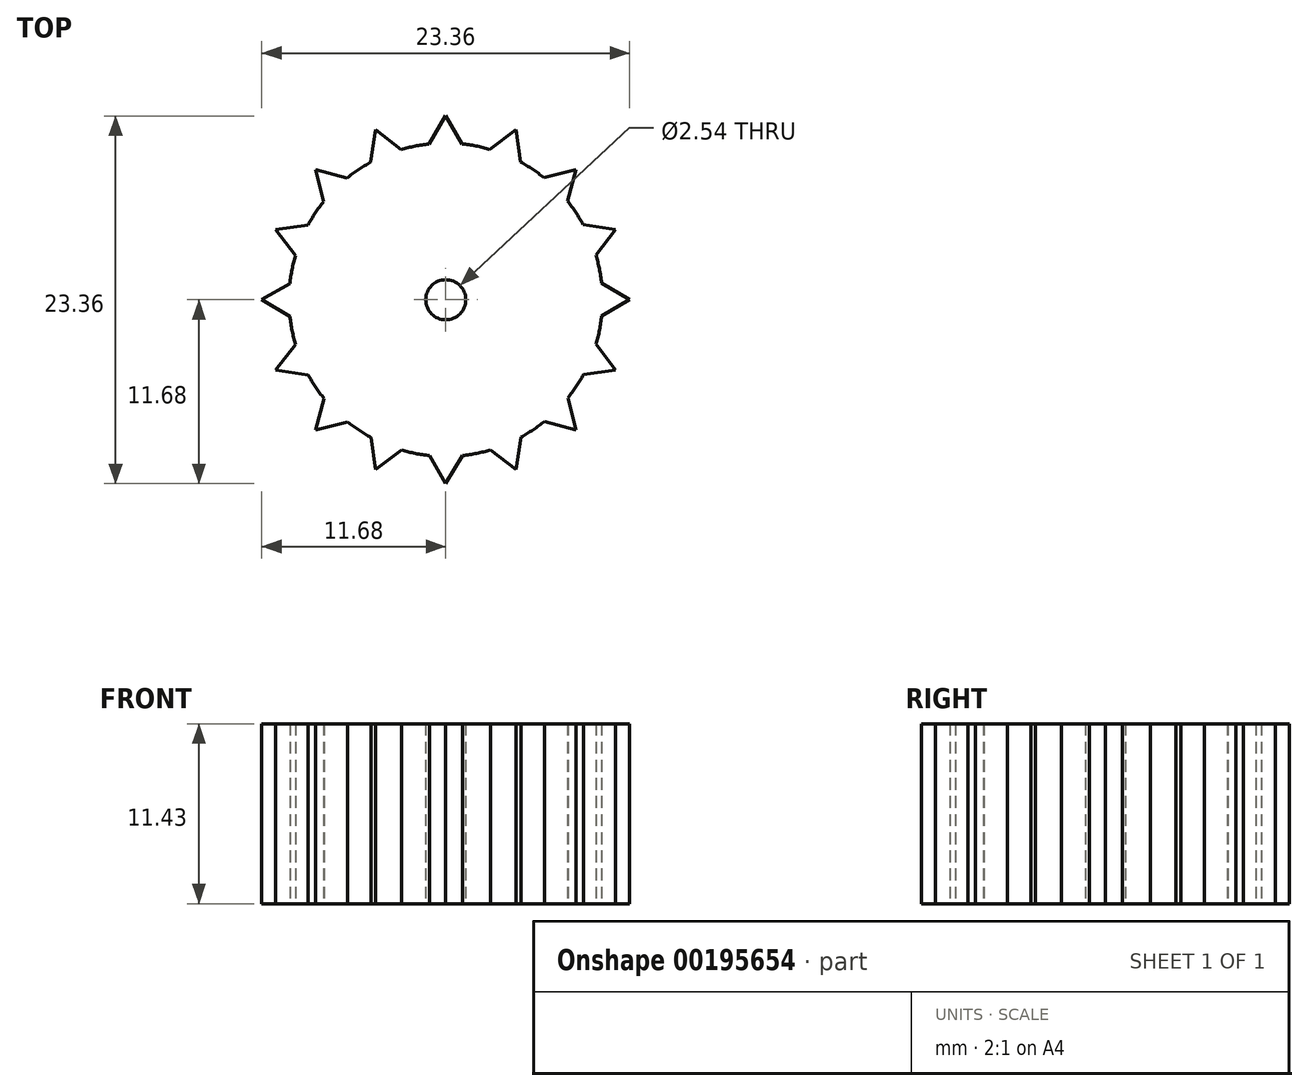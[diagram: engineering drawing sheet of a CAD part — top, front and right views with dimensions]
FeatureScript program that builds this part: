
annotation { "Feature Type Name" : "Feature", "Feature Type Description" : "" }
export const myFeature = defineFeature(function(context is Context, id is Id, definition is map)
    precondition{}
    {
        {
            var Q0;
            Q0=qCreatedBy(makeId("Top.planeOp"),FACE);
            var sketch = newSketch(context, id + "F0", { "sketchPlane" : qUnion([Q0])});
            skCircle(sketch, "E0", {"center": v(0, 0) * mm, "radius": 11.68 * mm});
            skCircle(sketch, "E1", {"center": v(0, 0) * mm, "radius": 1.27 * mm});
            skCircle(sketch, "E2", {"center": v(0, 0) * mm, "radius": 9.95 * mm});
            skLineSegment(sketch, "E3", {"start": v(0, 11.68) * mm, "end": v(-1.07, 9.9) * mm});
            skLineSegment(sketch, "E4", {"start": v(0, 11.68) * mm, "end": v(1.02, 9.9) * mm});
            skLineSegment(sketch, "E5.1.0", {"start": v(4.47, 10.8) * mm, "end": v(2.8, 9.55) * mm});
            skLineSegment(sketch, "E5.1.1", {"start": v(4.47, 10.8) * mm, "end": v(4.74, 8.75) * mm});
            skLineSegment(sketch, "E5.2.0", {"start": v(8.26, 8.26) * mm, "end": v(6.24, 7.75) * mm});
            skLineSegment(sketch, "E5.2.1", {"start": v(8.26, 8.26) * mm, "end": v(7.72, 6.28) * mm});
            skLineSegment(sketch, "E5.3.0", {"start": v(10.8, 4.47) * mm, "end": v(8.73, 4.78) * mm});
            skLineSegment(sketch, "E5.3.1", {"start": v(10.8, 4.47) * mm, "end": v(9.54, 2.84) * mm});
            skLineSegment(sketch, "E5.4.0", {"start": v(11.68, 0) * mm, "end": v(9.9, 1.07) * mm});
            skLineSegment(sketch, "E5.4.1", {"start": v(11.68, 0) * mm, "end": v(9.9, -1.02) * mm});
            skLineSegment(sketch, "E5.5.0", {"start": v(10.8, -4.47) * mm, "end": v(9.55, -2.8) * mm});
            skLineSegment(sketch, "E5.5.1", {"start": v(10.8, -4.47) * mm, "end": v(8.75, -4.74) * mm});
            skLineSegment(sketch, "E5.6.0", {"start": v(8.26, -8.26) * mm, "end": v(7.75, -6.24) * mm});
            skLineSegment(sketch, "E5.6.1", {"start": v(8.26, -8.26) * mm, "end": v(6.28, -7.72) * mm});
            skLineSegment(sketch, "E5.7.0", {"start": v(4.47, -10.8) * mm, "end": v(4.78, -8.73) * mm});
            skLineSegment(sketch, "E5.7.1", {"start": v(4.47, -10.8) * mm, "end": v(2.84, -9.54) * mm});
            skLineSegment(sketch, "E5.8.0", {"start": v(0, -11.68) * mm, "end": v(1.07, -9.9) * mm});
            skLineSegment(sketch, "E5.8.1", {"start": v(0, -11.68) * mm, "end": v(-1.02, -9.9) * mm});
            skLineSegment(sketch, "E5.9.0", {"start": v(-4.47, -10.8) * mm, "end": v(-2.8, -9.55) * mm});
            skLineSegment(sketch, "E5.9.1", {"start": v(-4.47, -10.8) * mm, "end": v(-4.74, -8.75) * mm});
            skLineSegment(sketch, "E5.10.0", {"start": v(-8.26, -8.26) * mm, "end": v(-6.24, -7.75) * mm});
            skLineSegment(sketch, "E5.10.1", {"start": v(-8.26, -8.26) * mm, "end": v(-7.72, -6.28) * mm});
            skLineSegment(sketch, "E5.11.0", {"start": v(-10.8, -4.47) * mm, "end": v(-8.73, -4.78) * mm});
            skLineSegment(sketch, "E5.11.1", {"start": v(-10.8, -4.47) * mm, "end": v(-9.54, -2.84) * mm});
            skLineSegment(sketch, "E5.12.0", {"start": v(-11.68, 0) * mm, "end": v(-9.9, -1.07) * mm});
            skLineSegment(sketch, "E5.12.1", {"start": v(-11.68, 0) * mm, "end": v(-9.9, 1.02) * mm});
            skLineSegment(sketch, "E5.13.0", {"start": v(-10.8, 4.47) * mm, "end": v(-9.55, 2.8) * mm});
            skLineSegment(sketch, "E5.13.1", {"start": v(-10.8, 4.47) * mm, "end": v(-8.75, 4.74) * mm});
            skLineSegment(sketch, "E5.14.0", {"start": v(-8.26, 8.26) * mm, "end": v(-7.75, 6.24) * mm});
            skLineSegment(sketch, "E5.14.1", {"start": v(-8.26, 8.26) * mm, "end": v(-6.28, 7.72) * mm});
            skLineSegment(sketch, "E5.15.0", {"start": v(-4.47, 10.8) * mm, "end": v(-4.78, 8.73) * mm});
            skLineSegment(sketch, "E5.15.1", {"start": v(-4.47, 10.8) * mm, "end": v(-2.84, 9.54) * mm});
            skLineSegment(sketch, "E5.anchor1", {"start": v(0, 0) * mm, "end": v(-1.07, 9.9) * mm, "construction": true});
            skLineSegment(sketch, "E5.anchor2", {"start": v(0, 0) * mm, "end": v(-4.78, 8.73) * mm, "construction": true});
            skSolve(sketch);
        }
        {
            var Q0;
            Q0=makeQuery(id+"F0.imprint","IMPRINT",FACE,{"disambiguationData":[TD([[makeQuery(id+"F0.imprint","IMPRINT",EDGE,{"derivedFrom":sQuery(id+"F0.wireOp",EDGE,"E1")}),-1.0]])]});
            var Q1;
            {var subQ0=sQuery(id+"F0.wireOp",EDGE,"E5.15.0");Q1=makeQuery(id+"F0.imprint","IMPRINT",FACE,{"disambiguationData":[TD([[makeQuery(id+"F0.imprint","IMPRINT",EDGE,{"derivedFrom":subQ0}),1.0]])]});}
            var Q2;
            {var subQ0=sQuery(id+"F0.wireOp",EDGE,"E3");Q2=makeQuery(id+"F0.imprint","IMPRINT",FACE,{"disambiguationData":[TD([[makeQuery(id+"F0.imprint","IMPRINT",EDGE,{"derivedFrom":subQ0}),1.0]])]});}
            var Q3;
            {var subQ0=sQuery(id+"F0.wireOp",EDGE,"E5.1.0");Q3=makeQuery(id+"F0.imprint","IMPRINT",FACE,{"disambiguationData":[TD([[makeQuery(id+"F0.imprint","IMPRINT",EDGE,{"derivedFrom":subQ0}),1.0]])]});}
            var Q4;
            {var subQ0=sQuery(id+"F0.wireOp",EDGE,"E5.2.0");Q4=makeQuery(id+"F0.imprint","IMPRINT",FACE,{"disambiguationData":[TD([[makeQuery(id+"F0.imprint","IMPRINT",EDGE,{"derivedFrom":subQ0}),1.0]])]});}
            var Q5;
            {var subQ0=sQuery(id+"F0.wireOp",EDGE,"E5.3.0");Q5=makeQuery(id+"F0.imprint","IMPRINT",FACE,{"disambiguationData":[TD([[makeQuery(id+"F0.imprint","IMPRINT",EDGE,{"derivedFrom":subQ0}),1.0]])]});}
            var Q6;
            {var subQ0=sQuery(id+"F0.wireOp",EDGE,"E5.4.0");Q6=makeQuery(id+"F0.imprint","IMPRINT",FACE,{"disambiguationData":[TD([[makeQuery(id+"F0.imprint","IMPRINT",EDGE,{"derivedFrom":subQ0}),1.0]])]});}
            var Q7;
            {var subQ0=sQuery(id+"F0.wireOp",EDGE,"E5.5.0");Q7=makeQuery(id+"F0.imprint","IMPRINT",FACE,{"disambiguationData":[TD([[makeQuery(id+"F0.imprint","IMPRINT",EDGE,{"derivedFrom":subQ0}),1.0]])]});}
            var Q8;
            {var subQ0=sQuery(id+"F0.wireOp",EDGE,"E5.6.0");Q8=makeQuery(id+"F0.imprint","IMPRINT",FACE,{"disambiguationData":[TD([[makeQuery(id+"F0.imprint","IMPRINT",EDGE,{"derivedFrom":subQ0}),1.0]])]});}
            var Q9;
            {var subQ0=sQuery(id+"F0.wireOp",EDGE,"E5.7.0");Q9=makeQuery(id+"F0.imprint","IMPRINT",FACE,{"disambiguationData":[TD([[makeQuery(id+"F0.imprint","IMPRINT",EDGE,{"derivedFrom":subQ0}),1.0]])]});}
            var Q10;
            {var subQ0=sQuery(id+"F0.wireOp",EDGE,"E5.8.0");Q10=makeQuery(id+"F0.imprint","IMPRINT",FACE,{"disambiguationData":[TD([[makeQuery(id+"F0.imprint","IMPRINT",EDGE,{"derivedFrom":subQ0}),1.0]])]});}
            var Q11;
            {var subQ0=sQuery(id+"F0.wireOp",EDGE,"E5.9.0");Q11=makeQuery(id+"F0.imprint","IMPRINT",FACE,{"disambiguationData":[TD([[makeQuery(id+"F0.imprint","IMPRINT",EDGE,{"derivedFrom":subQ0}),1.0]])]});}
            var Q12;
            {var subQ0=sQuery(id+"F0.wireOp",EDGE,"E5.10.0");Q12=makeQuery(id+"F0.imprint","IMPRINT",FACE,{"disambiguationData":[TD([[makeQuery(id+"F0.imprint","IMPRINT",EDGE,{"derivedFrom":subQ0}),1.0]])]});}
            var Q13;
            {var subQ0=sQuery(id+"F0.wireOp",EDGE,"E5.11.0");Q13=makeQuery(id+"F0.imprint","IMPRINT",FACE,{"disambiguationData":[TD([[makeQuery(id+"F0.imprint","IMPRINT",EDGE,{"derivedFrom":subQ0}),1.0]])]});}
            var Q14;
            {var subQ0=sQuery(id+"F0.wireOp",EDGE,"E5.12.0");Q14=makeQuery(id+"F0.imprint","IMPRINT",FACE,{"disambiguationData":[TD([[makeQuery(id+"F0.imprint","IMPRINT",EDGE,{"derivedFrom":subQ0}),1.0]])]});}
            var Q15;
            {var subQ0=sQuery(id+"F0.wireOp",EDGE,"E5.13.0");Q15=makeQuery(id+"F0.imprint","IMPRINT",FACE,{"disambiguationData":[TD([[makeQuery(id+"F0.imprint","IMPRINT",EDGE,{"derivedFrom":subQ0}),1.0]])]});}
            var Q16;
            {var subQ0=sQuery(id+"F0.wireOp",EDGE,"E5.14.0");Q16=makeQuery(id+"F0.imprint","IMPRINT",FACE,{"disambiguationData":[TD([[makeQuery(id+"F0.imprint","IMPRINT",EDGE,{"derivedFrom":subQ0}),1.0]])]});}
            extrude(context, id + "F1", {"entities" : qUnion([Q0, Q1, Q2, Q3, Q4, Q5, Q6, Q7, Q8, Q9, Q10, Q11, Q12, Q13, Q14, Q15, Q16]), "depth" : 11.43 * mm});
        }
    });
